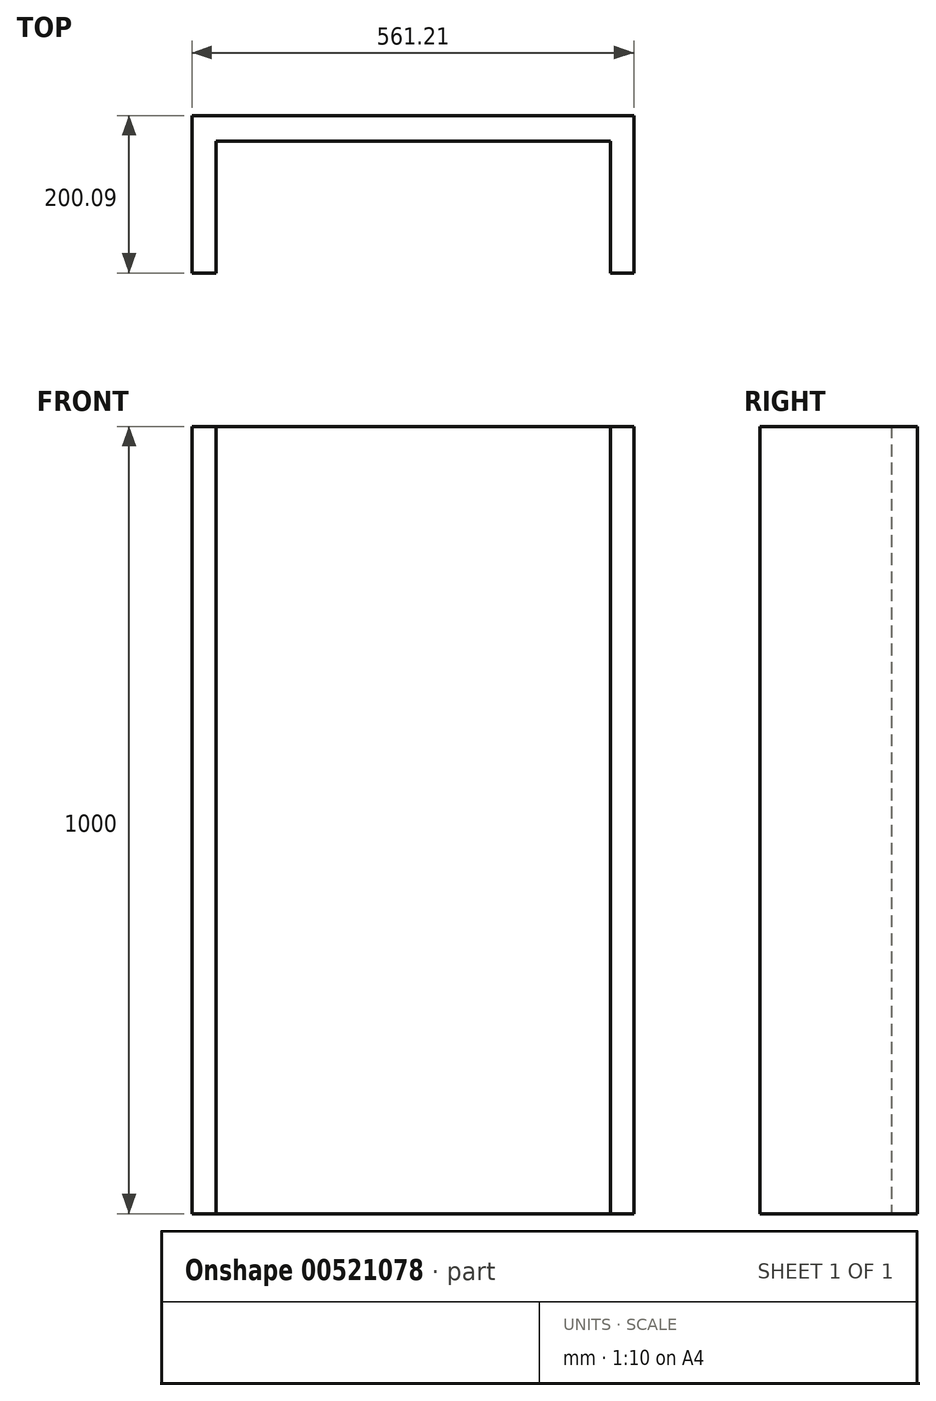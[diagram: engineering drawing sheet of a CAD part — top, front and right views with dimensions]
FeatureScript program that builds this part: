
annotation { "Feature Type Name" : "Feature", "Feature Type Description" : "" }
export const myFeature = defineFeature(function(context is Context, id is Id, definition is map)
    precondition{}
    {
        {
            var Q0;
            Q0=qCreatedBy(makeId("Top.planeOp"),FACE);
            var sketch = newSketch(context, id + "F0", { "sketchPlane" : qUnion([Q0])});
            skLineSegment(sketch, "E0.bottom", {"start": v(148.44, 33.7) * mm, "end": v(-352.74, 33.7) * mm});
            skLineSegment(sketch, "E0.top", {"start": v(148.44, 0.81) * mm, "end": v(-352.74, 0.81) * mm});
            skLineSegment(sketch, "E0.left", {"start": v(148.44, 33.7) * mm, "end": v(148.44, 0.81) * mm});
            skLineSegment(sketch, "E0.right", {"start": v(-352.74, 33.7) * mm, "end": v(-352.74, 0.81) * mm});
            skPoint(sketch, "E0.middle", {"position": v(-102.15, 17.25) * mm});
            skLineSegment(sketch, "E1.bottom", {"start": v(-352.74, 33.7) * mm, "end": v(-383.23, 33.7) * mm});
            skLineSegment(sketch, "E1.top", {"start": v(-352.74, -166.4) * mm, "end": v(-383.23, -166.4) * mm});
            skLineSegment(sketch, "E1.left", {"start": v(-352.74, 33.7) * mm, "end": v(-352.74, -166.4) * mm});
            skLineSegment(sketch, "E1.right", {"start": v(-383.23, 33.7) * mm, "end": v(-383.23, -166.4) * mm});
            skLineSegment(sketch, "E2.bottom", {"start": v(148.44, 33.7) * mm, "end": v(177.98, 33.7) * mm});
            skLineSegment(sketch, "E2.top", {"start": v(148.44, -166.4) * mm, "end": v(177.98, -166.4) * mm});
            skLineSegment(sketch, "E2.left", {"start": v(148.44, 33.7) * mm, "end": v(148.44, -166.4) * mm});
            skLineSegment(sketch, "E2.right", {"start": v(177.98, 33.7) * mm, "end": v(177.98, -166.4) * mm});
            skSolve(sketch);
        }
        {
            var Q0;
            {var subQ3=sQuery(id+"F0.wireOp",EDGE,"E1.bottom");Q0=makeQuery(id+"F0.imprint","IMPRINT",FACE,{"disambiguationData":[TD([[makeQuery(id+"F0.imprint","IMPRINT",EDGE,{"derivedFrom":subQ3}),1.0]])]});}
            var Q1;
            {var subQ0=sQuery(id+"F0.wireOp",EDGE,"E0.bottom");Q1=makeQuery(id+"F0.imprint","IMPRINT",FACE,{"disambiguationData":[TD([[makeQuery(id+"F0.imprint","IMPRINT",EDGE,{"derivedFrom":subQ0}),1.0]])]});}
            var Q2;
            {var subQ3=sQuery(id+"F0.wireOp",EDGE,"E2.bottom");Q2=makeQuery(id+"F0.imprint","IMPRINT",FACE,{"disambiguationData":[TD([[makeQuery(id+"F0.imprint","IMPRINT",EDGE,{"derivedFrom":subQ3}),-1.0]])]});}
            extrude(context, id + "F1", {"entities" : qUnion([Q0, Q1, Q2]), "depth" : 1000 * mm, "offsetDistance" : 25 * mm});
        }
    });
